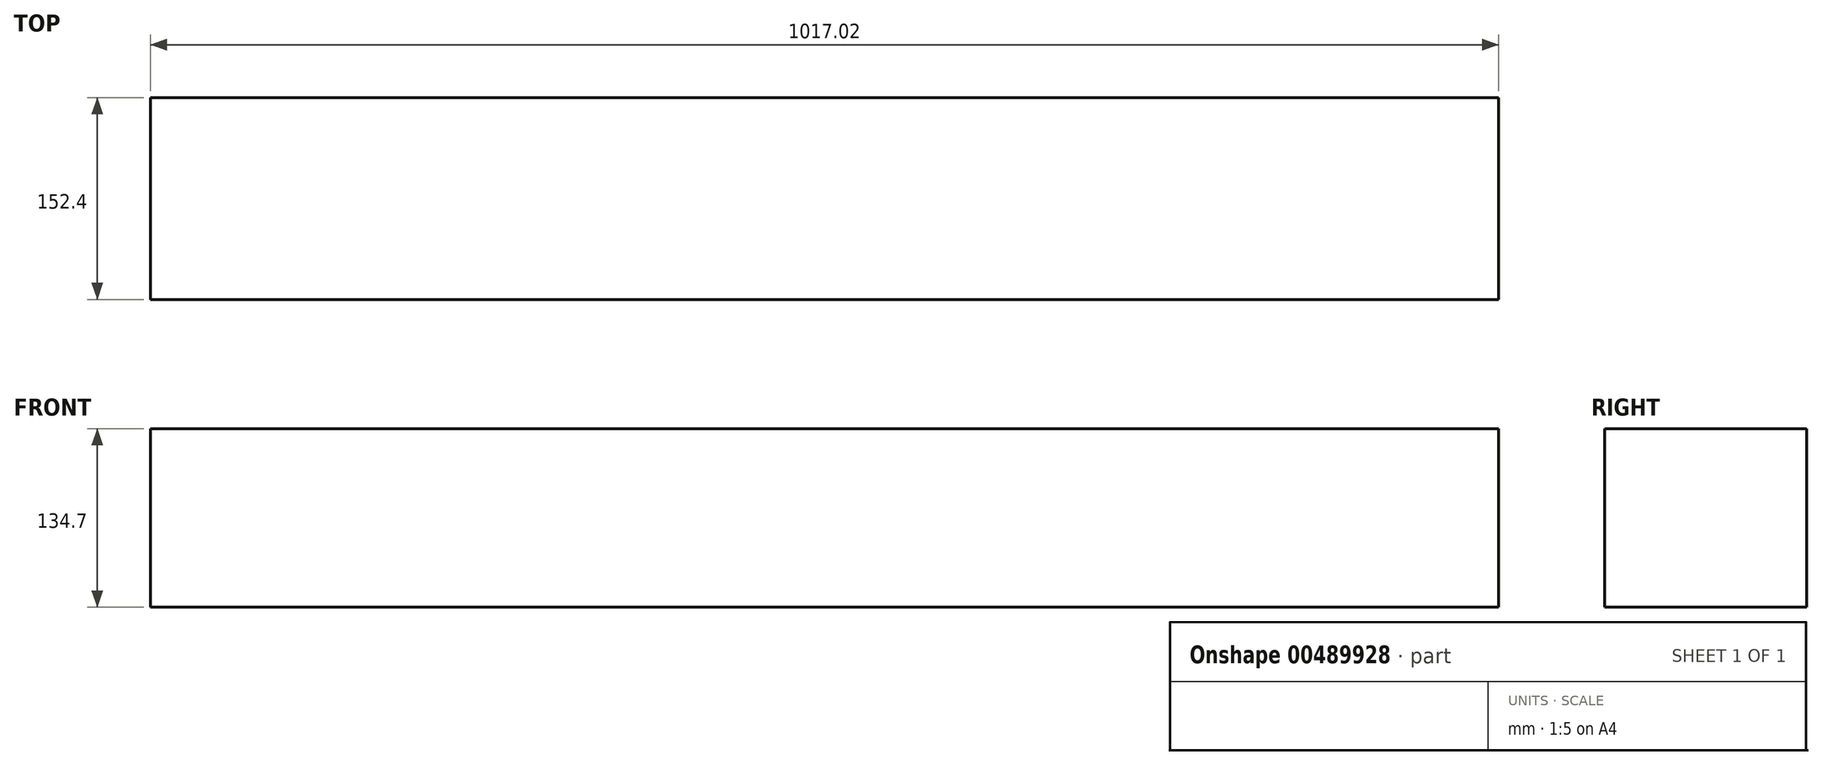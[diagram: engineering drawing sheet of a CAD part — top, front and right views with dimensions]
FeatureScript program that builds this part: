
annotation { "Feature Type Name" : "Feature", "Feature Type Description" : "" }
export const myFeature = defineFeature(function(context is Context, id is Id, definition is map)
    precondition{}
    {
        {
            var Q0;
            Q0=qCreatedBy(makeId("Front.planeOp"),FACE);
            var sketch = newSketch(context, id + "F0", { "sketchPlane" : qUnion([Q0])});
            skLineSegment(sketch, "E0.bottom", {"start": v(127.5, 67.35) * mm, "end": v(-127.5, 67.35) * mm});
            skLineSegment(sketch, "E0.top", {"start": v(127.5, -67.35) * mm, "end": v(-127.5, -67.35) * mm});
            skLineSegment(sketch, "E0.left", {"start": v(127.5, 67.35) * mm, "end": v(127.5, -67.35) * mm});
            skLineSegment(sketch, "E0.right", {"start": v(-127.5, 67.35) * mm, "end": v(-127.5, -67.35) * mm});
            skPoint(sketch, "E0.middle", {"position": v(0, 0) * mm});
            skSolve(sketch);
        }
        {
            var Q0;
            Q0=makeQuery(id+"F0.imprint","IMPRINT",FACE,{"disambiguationData":[TD([[makeQuery(id+"F0.imprint","IMPRINT",EDGE,{"derivedFrom":sQuery(id+"F0.wireOp",EDGE,"E0.bottom")}),1.0]])]});
            extrude(context, id + "F1", {"entities" : qUnion([Q0]), "depth" : 152.4 * mm});
        }
        {
            var Q0;
            Q0=makeQuery(id+"F1.opExtrude","SWEPT_FACE",FACE,{"disambiguationData":[OSD([sQuery(id+"F0.wireOp",EDGE,"E0.left")])]});
            extrude(context, id + "F2", {"entities" : qUnion([Q0]), "operationType" : NewBodyOperationType.ADD, "depth" : 381 * mm});
        }
        {
            var Q0;
            Q0=makeQuery(id+"F1.opExtrude","SWEPT_FACE",FACE,{"disambiguationData":[OSD([sQuery(id+"F0.wireOp",EDGE,"E0.right")])]});
            extrude(context, id + "F3", {"entities" : qUnion([Q0]), "operationType" : NewBodyOperationType.ADD, "depth" : 381 * mm});
        }
    });
